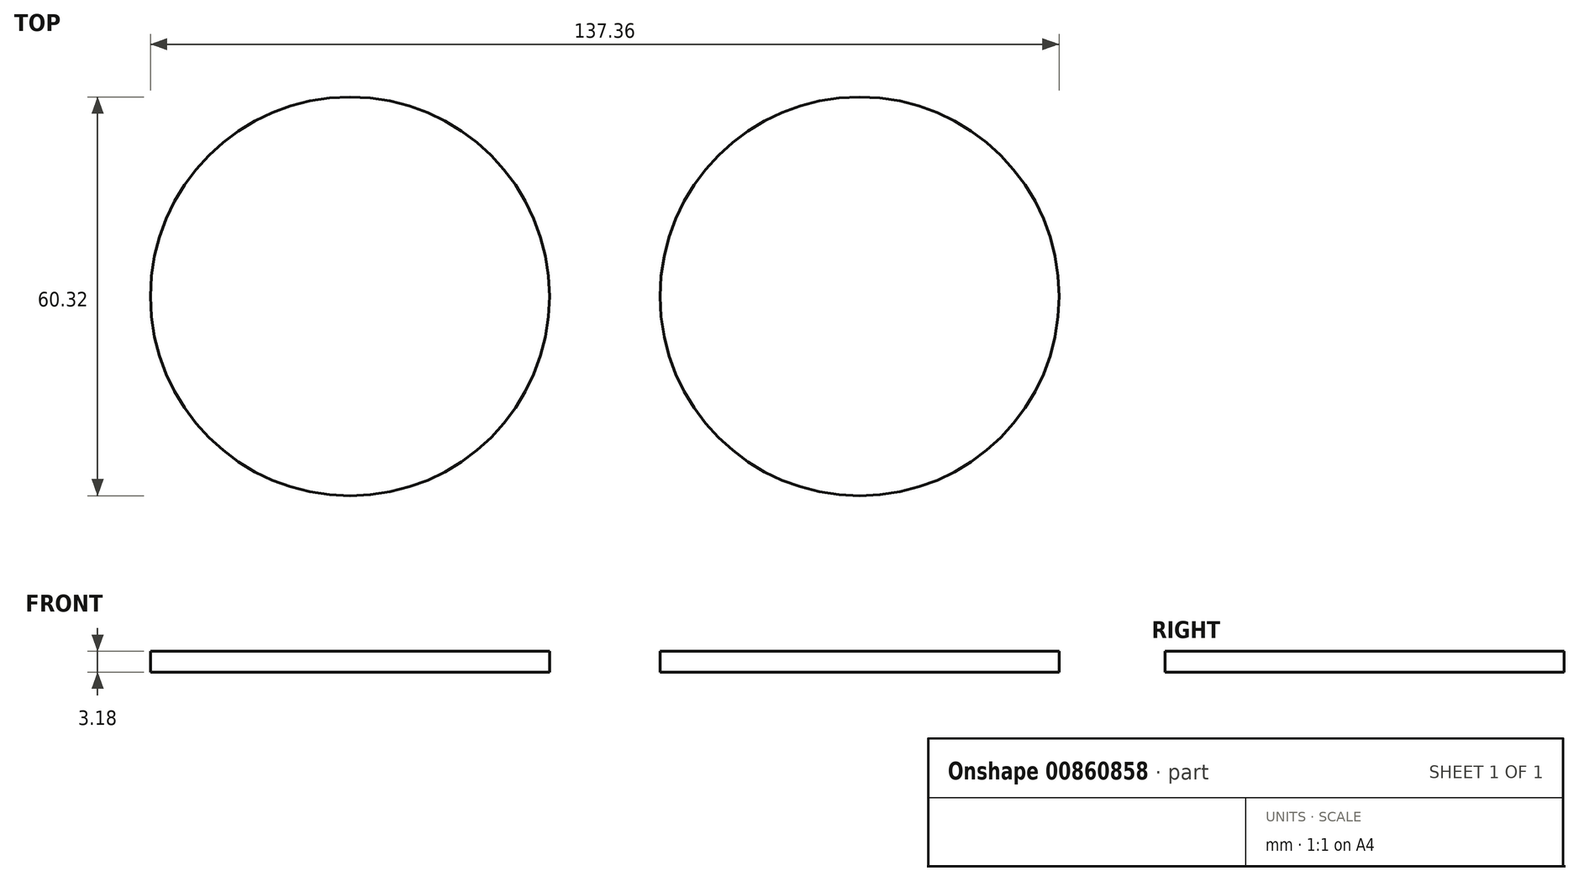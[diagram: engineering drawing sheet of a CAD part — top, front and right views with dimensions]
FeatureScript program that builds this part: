
annotation { "Feature Type Name" : "Feature", "Feature Type Description" : "" }
export const myFeature = defineFeature(function(context is Context, id is Id, definition is map)
    precondition{}
    {
        {
            var Q0;
            Q0=qCreatedBy(makeId("Top.planeOp"),FACE);
            var sketch = newSketch(context, id + "F0", { "sketchPlane" : qUnion([Q0])});
            skCircle(sketch, "E0", {"center": v(0, 0) * mm, "radius": 30.16 * mm});
            skCircle(sketch, "E1", {"center": v(-77.04, 0) * mm, "radius": 30.16 * mm});
            skSolve(sketch);
        }
        {
            var Q0;
            Q0=makeQuery(id+"F0.imprint","IMPRINT",FACE,{"disambiguationData":[TD([[makeQuery(id+"F0.imprint","IMPRINT",EDGE,{"derivedFrom":sQuery(id+"F0.wireOp",EDGE,"E1")}),1.0]])]});
            var Q1;
            Q1=makeQuery(id+"F0.imprint","IMPRINT",FACE,{"disambiguationData":[TD([[makeQuery(id+"F0.imprint","IMPRINT",EDGE,{"derivedFrom":sQuery(id+"F0.wireOp",EDGE,"E0")}),1.0]])]});
            extrude(context, id + "F1", {"entities" : qUnion([Q0, Q1]), "depth" : 3.17 * mm, "offsetDistance" : 25.4 * mm});
        }
    });
